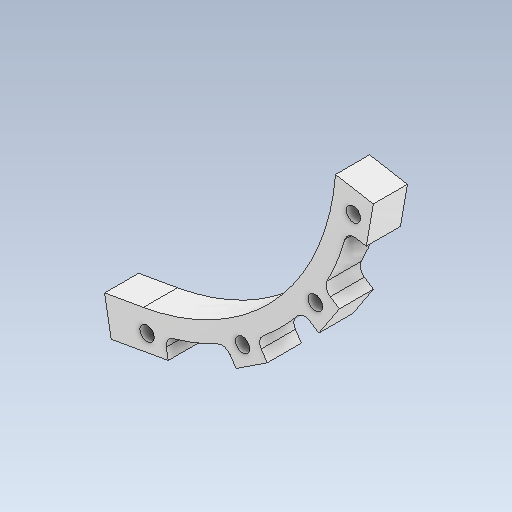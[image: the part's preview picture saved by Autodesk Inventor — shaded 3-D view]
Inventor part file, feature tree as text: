
AUTODESK INVENTOR PART (.ipt)
format: ipt  version: 2020 (Build 240168000, 168)  size: 197,120 bytes
history: native  units: mm
features: reference x7, other x5, sketch x3, extrude x2, hole x1, fillet x1
ambient origin geometry x8: Origin, YZ Plane, XZ Plane, XY Plane, X Axis, Y Axis, Z Axis, Center Point
bodies: Solid1 (feature_tree)
feature tree (19):
  extrude  "Extrusion1"  Depth=108.0mm
  extrude  "Extrusion2"  Depth=8.0mm
  hole  "Hole1"  [1 undecoded]
  fillet  "Fillet1"  Radius=7.3mm
  sketch  "Sketch1"  dims[d0=100.0mm d1=108.0mm]
  reference  "Reference1"
  reference  "Reference2"
  sketch  "Sketch2"  dims[d2=7.3mm d3=0.0mm d4=8.0mm]
  reference  "Reference3"
  sketch  "Sketch3"  dims[d5=7.0mm d6=40.0mm d8=12.217305mm d10=7.3mm d11=0.0mm d12=3.1mm d13=6.0mm d14=4.0mm d15=2.0mm d16=90.0deg d17=17.0mm d18=0.0mm d19=2.0mm]
  reference  "Reference4"
  reference  "Reference5"
  reference  "Reference6"
  reference  "Reference7"
  parser-record x1  (decoder bookkeeping rows leaked as tree rows — omitted from the tree; the rows remain in map.json)
  other  "reducer_2.iam"
  other  "motor_h_2:1"
  other  "90_motor:1"
  other  "90motor_top:1"
note: 1 required parameter value undecoded (feature->parameter linkage not recoverable at this tier; creation-order binding heuristic only, values carry confidence <= 0.55)
note: 1 file-system path scrubbed to <path> (originals preserved in map.json)
